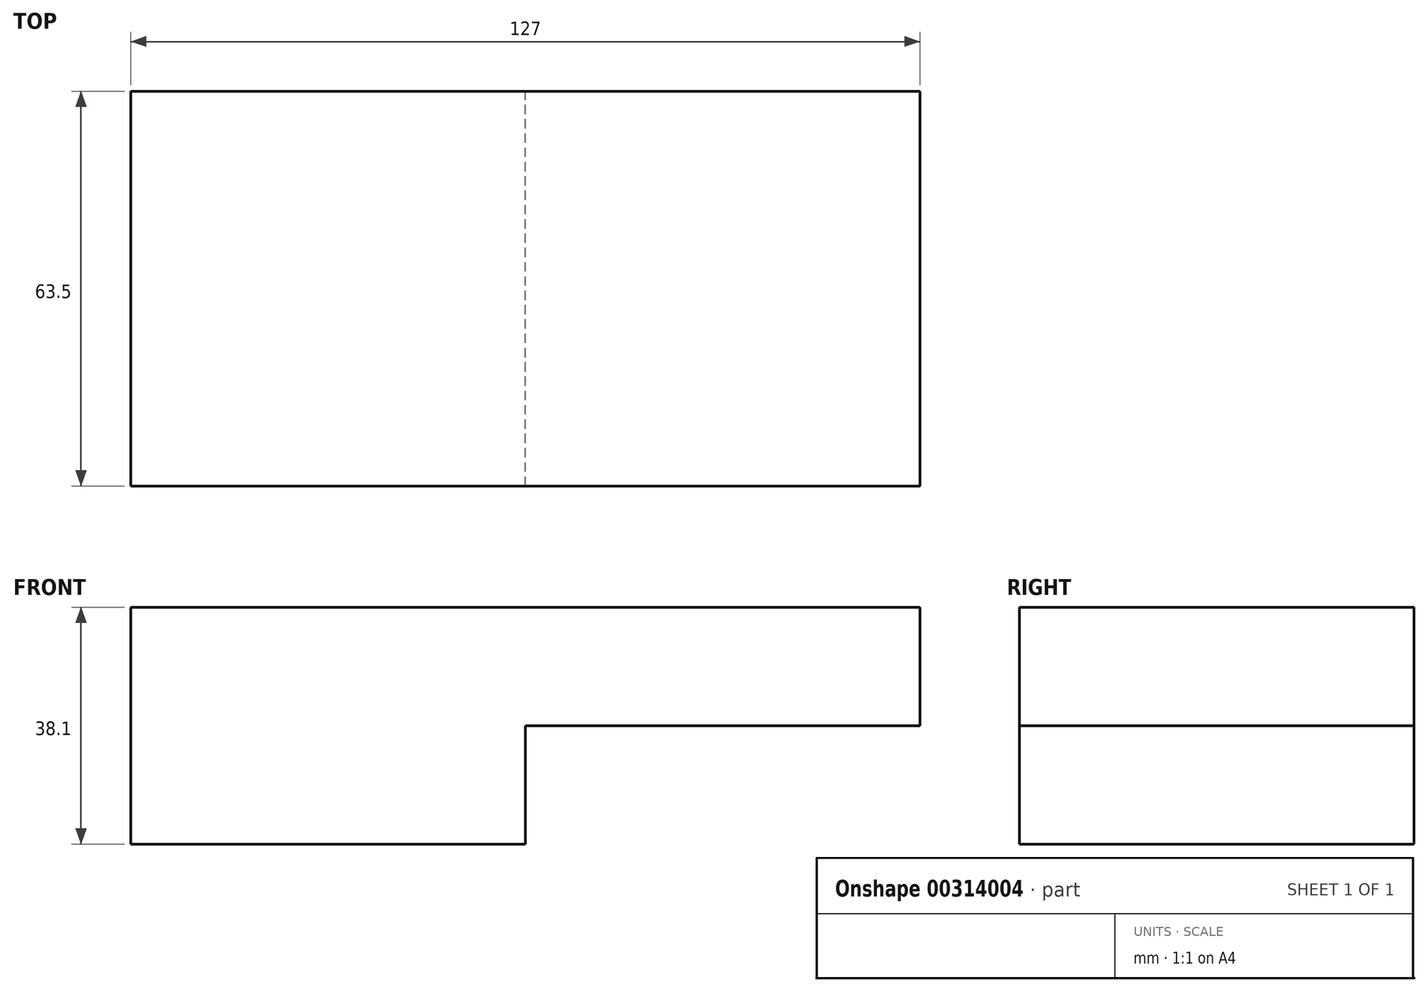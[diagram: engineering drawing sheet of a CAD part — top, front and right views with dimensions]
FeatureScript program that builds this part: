
annotation { "Feature Type Name" : "Feature", "Feature Type Description" : "" }
export const myFeature = defineFeature(function(context is Context, id is Id, definition is map)
    precondition{}
    {
        {
            var Q0;
            Q0=qCreatedBy(makeId("Front.planeOp"),FACE);
            var sketch = newSketch(context, id + "F0", { "sketchPlane" : qUnion([Q0])});
            skLineSegment(sketch, "E0", {"start": v(-73.48, 41.75) * mm, "end": v(53.52, 41.75) * mm});
            skLineSegment(sketch, "E1", {"start": v(53.52, 41.75) * mm, "end": v(53.52, 22.7) * mm});
            skLineSegment(sketch, "E2", {"start": v(53.52, 22.7) * mm, "end": v(-9.98, 22.7) * mm});
            skLineSegment(sketch, "E3", {"start": v(-9.98, 22.7) * mm, "end": v(-9.98, 3.65) * mm});
            skLineSegment(sketch, "E4", {"start": v(-9.98, 3.65) * mm, "end": v(-73.48, 3.65) * mm});
            skLineSegment(sketch, "E5", {"start": v(-73.48, 41.75) * mm, "end": v(-73.48, 3.65) * mm});
            skSolve(sketch);
        }
        {
            var Q0;
            Q0=makeQuery(id+"F0.imprint","IMPRINT",FACE,{"disambiguationData":[TD([[makeQuery(id+"F0.imprint","IMPRINT",EDGE,{"derivedFrom":sQuery(id+"F0.wireOp",EDGE,"E0")}),-1.0]])]});
            extrude(context, id + "F1", {"entities" : qUnion([Q0]), "depth" : 63.5 * mm});
        }
    });
